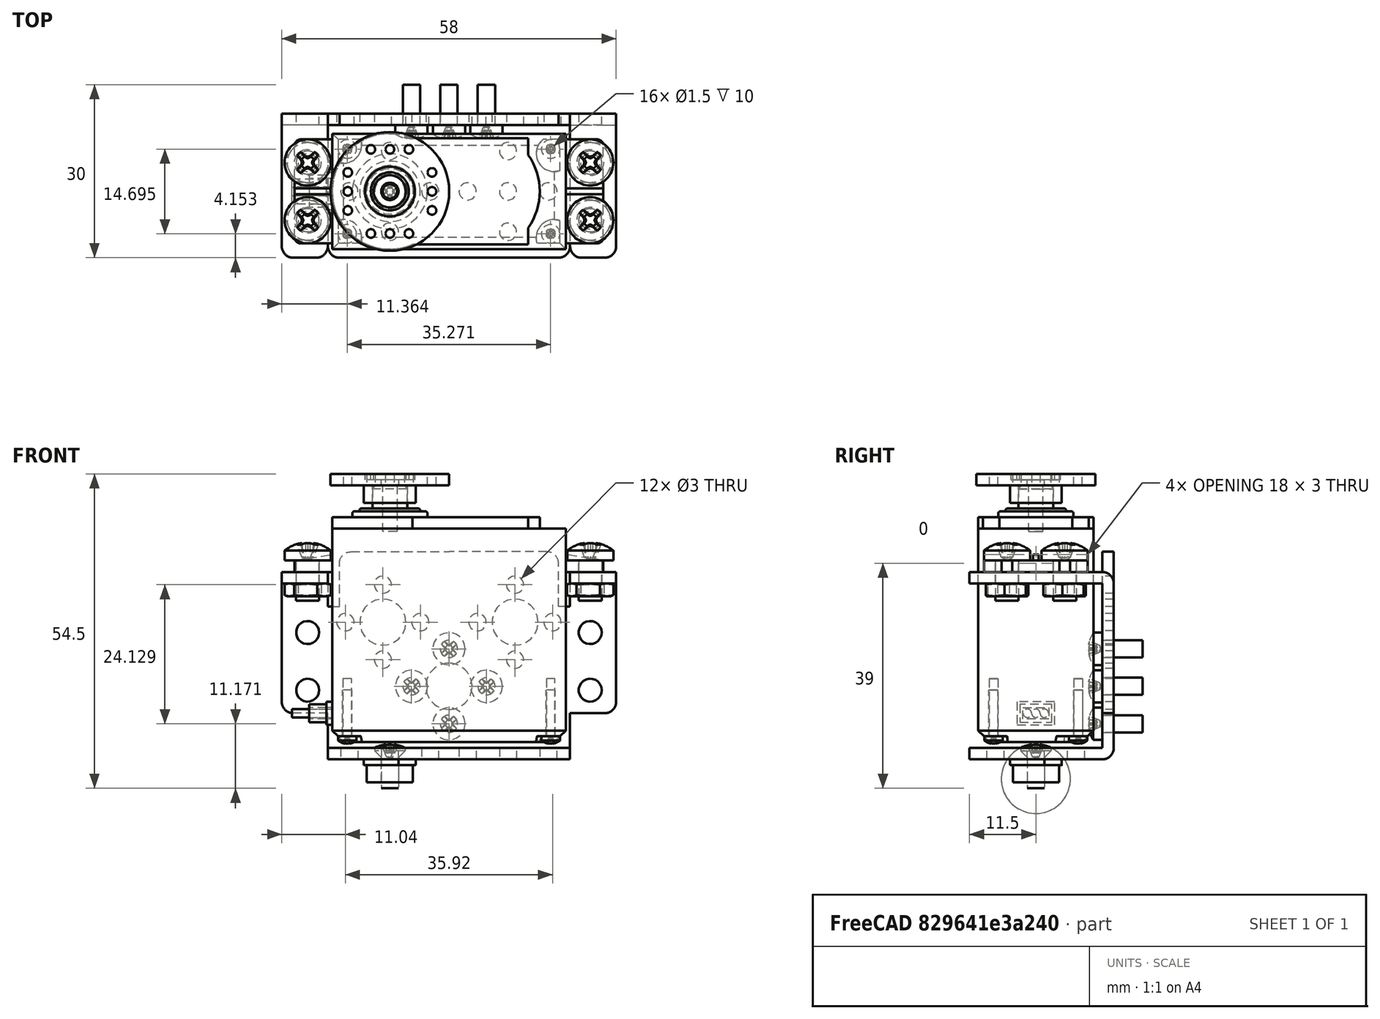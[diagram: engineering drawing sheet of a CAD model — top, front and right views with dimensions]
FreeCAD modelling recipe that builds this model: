
FCSTD DOCUMENT  (FreeCAD 0.19R24276 (Git))
Label: servo_acoplado_1
License: All rights reserved
LicenseURL: http://en.wikipedia.org/wiki/All_rights_reserved
objects: Part::FeaturePython×17, App::FeaturePython×12, App::DocumentObjectGroup×2
note: 17 computed .brp shape members not serialized (recipe doc carries the construction recipe); baked Part::Feature solids carry a one-line shape summary decoded from their .brp

FEATURE [Part::FeaturePython] b_servo_001_  label="servo_001"  # a2plus imported part (geometry in sourceFile) (typed FeaturePython)
  a2p_Version = V0.1
  fixedPosition = true
  objectType = a2pPart
  sourceFile = .\..\piezas\servo.FCStd
  subassemblyImport = false
  timeLastImport = 1.62041e+09
  updateColors = true
FEATURE [Part::FeaturePython] b_parte_servos_001_  label="parte_servos_001"  # a2plus imported part (geometry in sourceFile) (typed FeaturePython)
  Placement = pos=(2.597e-07,13.5,15) rot=(1,0,0;1.5708rad)
  a2p_Version = V0.1
  fixedPosition = false
  objectType = a2pPart
  sourceFile = .\..\piezas\parte_servos.FCStd
  subassemblyImport = false
  timeLastImport = 1.62041e+09
  updateColors = true
FEATURE [Part::FeaturePython] b_arandela_001_  label="arandela_001"  # a2plus imported part (geometry in sourceFile) (typed FeaturePython)
  Placement = pos=(-10.25,3.87576e-07,-3) rot=(0,1,0;3.14159rad)
  a2p_Version = V0.1
  fixedPosition = false
  objectType = a2pPart
  sourceFile = .\..\piezas\arandela.FCStd
  subassemblyImport = false
  timeLastImport = 1.62041e+09
  updateColors = true
FEATURE [Part::FeaturePython] b_tapa_001_  label="tapa_001"  # a2plus imported part (geometry in sourceFile) (typed FeaturePython)
  Placement = pos=(-10.25,-6.8e-14,46.5) rot=(1,0,0;3.14159rad)
  a2p_Version = V0.1
  fixedPosition = false
  objectType = a2pPart
  sourceFile = .\..\piezas\tapa.FCStd
  subassemblyImport = false
  timeLastImport = 1.62041e+09
  updateColors = true
FEATURE [App::FeaturePython] planeCoincident_001  label="planeCoincident_001__parte_servos_001"  # a2plus constraint (typed FeaturePython)
  Object1 = b_servo_001_
  Object2 = b_parte_servos_001_
  ParentTreeObject = -> b_servo_001_
  SubElement1 = Face61
  SubElement2 = Face84
  Suppressed = false
  Type = plane
  directionConstraint = 0
  offset = 0
FEATURE [App::FeaturePython] planeCoincident_001_mirror  label="planeCoincident_001__servo_001"  # a2plus constraint (typed FeaturePython)
  Object1 = b_servo_001_
  Object2 = b_parte_servos_001_
  ParentTreeObject = -> b_parte_servos_001_
  SubElement1 = Face61
  SubElement2 = Face84
  Suppressed = false
  Type = plane
  directionConstraint = 0
  offset = 0
FEATURE [App::FeaturePython] axisCoincident_001  label="axisCoincident_001__parte_servos_001"  # a2plus constraint (typed FeaturePython)
  Object1 = b_servo_001_
  Object2 = b_parte_servos_001_
  ParentTreeObject = -> b_servo_001_
  SubElement1 = Face84
  SubElement2 = Face82
  Suppressed = false
  Type = axial
  directionConstraint = 1
  lockRotation = false
FEATURE [App::FeaturePython] axisCoincident_001_mirror  label="axisCoincident_001__servo_001"  # a2plus constraint (typed FeaturePython)
  Object1 = b_servo_001_
  Object2 = b_parte_servos_001_
  ParentTreeObject = -> b_parte_servos_001_
  SubElement1 = Face84
  SubElement2 = Face82
  Suppressed = false
  Type = axial
  directionConstraint = 1
  lockRotation = false
FEATURE [App::FeaturePython] planeCoincident_002  label="planeCoincident_002__arandela_001"  # a2plus constraint (typed FeaturePython)
  Object1 = b_parte_servos_001_
  Object2 = b_arandela_001_
  ParentTreeObject = -> b_parte_servos_001_
  SubElement1 = Face4
  SubElement2 = Face2
  Suppressed = false
  Type = plane
  directionConstraint = 1
  offset = 0
FEATURE [App::FeaturePython] planeCoincident_002_mirror  label="planeCoincident_002__parte_servos_001"  # a2plus constraint (typed FeaturePython)
  Object1 = b_parte_servos_001_
  Object2 = b_arandela_001_
  ParentTreeObject = -> b_arandela_001_
  SubElement1 = Face4
  SubElement2 = Face2
  Suppressed = false
  Type = plane
  directionConstraint = 1
  offset = 0
FEATURE [App::FeaturePython] axisCoincident_002  label="axisCoincident_002__parte_servos_001"  # a2plus constraint (typed FeaturePython)
  Object1 = b_arandela_001_
  Object2 = b_parte_servos_001_
  ParentTreeObject = -> b_arandela_001_
  SubElement1 = Face4
  SubElement2 = Face17
  Suppressed = false
  Type = axial
  directionConstraint = 1
  lockRotation = false
FEATURE [App::FeaturePython] axisCoincident_002_mirror  label="axisCoincident_002__arandela_001"  # a2plus constraint (typed FeaturePython)
  Object1 = b_arandela_001_
  Object2 = b_parte_servos_001_
  ParentTreeObject = -> b_parte_servos_001_
  SubElement1 = Face4
  SubElement2 = Face17
  Suppressed = false
  Type = axial
  directionConstraint = 1
  lockRotation = false
FEATURE [App::FeaturePython] axisCoincident_003  label="axisCoincident_003__servo_001"  # a2plus constraint (typed FeaturePython)
  Object1 = b_tapa_001_
  Object2 = b_servo_001_
  ParentTreeObject = -> b_tapa_001_
  SubElement1 = Face21
  SubElement2 = Face141
  Suppressed = false
  Type = axial
  directionConstraint = 1
  lockRotation = false
FEATURE [App::FeaturePython] axisCoincident_003_mirror  label="axisCoincident_003__tapa_001"  # a2plus constraint (typed FeaturePython)
  Object1 = b_tapa_001_
  Object2 = b_servo_001_
  ParentTreeObject = -> b_servo_001_
  SubElement1 = Face21
  SubElement2 = Face141
  Suppressed = false
  Type = axial
  directionConstraint = 1
  lockRotation = false
FEATURE [App::FeaturePython] planeCoincident_003  label="planeCoincident_003__servo_001"  # a2plus constraint (typed FeaturePython)
  Object1 = b_tapa_001_
  Object2 = b_servo_001_
  ParentTreeObject = -> b_tapa_001_
  SubElement1 = Face23
  SubElement2 = Face34
  Suppressed = false
  Type = plane
  directionConstraint = 1
  offset = 0
FEATURE [App::FeaturePython] planeCoincident_003_mirror  label="planeCoincident_003__tapa_001"  # a2plus constraint (typed FeaturePython)
  Object1 = b_tapa_001_
  Object2 = b_servo_001_
  ParentTreeObject = -> b_servo_001_
  SubElement1 = Face23
  SubElement2 = Face34
  Suppressed = false
  Type = plane
  directionConstraint = 1
  offset = 0
FEATURE [Part::FeaturePython] Screw  label="M3x7-Screw"  # Fasteners workbench fastener (typed FeaturePython)
  Placement = pos=(-10.25,3.79261e-07,-1) rot=(0,0,1;0rad)
  baseObject = -> b_parte_servos_001_ [Edge75]
  diameter = 4
  invert = false
  length = 11
  lengthCustom = 7
  matchOuter = true
  offset = 0
  thread = false
  type = 36
FEATURE [Part::FeaturePython] Screw001  label="M4x7-Screw"  # Fasteners workbench fastener (typed FeaturePython)
  Placement = pos=(-24.5,5,31.5) rot=(0,0,1;0rad)
  baseObject = -> b_servo_001_ [Edge725]
  diameter = 6
  invert = true
  length = 12
  lengthCustom = 7
  matchOuter = true
  offset = 0
  thread = false
  type = 34
FEATURE [Part::FeaturePython] Screw002  label="M4x7-Screw004"  # Fasteners workbench fastener (typed FeaturePython)
  Placement = pos=(24.5,5,31.5) rot=(0,0,1;0rad)
  baseObject = -> b_servo_001_ [Edge159]
  diameter = 6
  invert = false
  length = 12
  lengthCustom = 7
  matchOuter = true
  offset = 0
  thread = false
  type = 34
FEATURE [Part::FeaturePython] Screw003  label="M4x7-Screw005"  # Fasteners workbench fastener (typed FeaturePython)
  Placement = pos=(24.5,-5,31.5) rot=(0,0,1;0rad)
  baseObject = -> b_servo_001_ [Edge173]
  diameter = 6
  invert = false
  length = 12
  lengthCustom = 7
  matchOuter = true
  offset = 0
  thread = false
  type = 34
FEATURE [Part::FeaturePython] Screw004  label="M4x7-Screw006"  # Fasteners workbench fastener (typed FeaturePython)
  Placement = pos=(-24.5,-5,31.5) rot=(0,0,1;0rad)
  baseObject = -> b_servo_001_ [Edge233]
  diameter = 6
  invert = true
  length = 12
  lengthCustom = 7
  matchOuter = true
  offset = 0
  thread = false
  type = 34
FEATURE [Part::FeaturePython] Nut  label="M4-Nut"  # Fasteners workbench fastener (typed FeaturePython)
  Placement = pos=(-24.5,5,27.5) rot=(-0.456083,0.889937,0;3.14159rad)
  baseObject = -> b_parte_servos_001_ [Edge193]
  diameter = 6
  invert = true
  matchOuter = true
  offset = 0
  thread = false
  type = 9
FEATURE [Part::FeaturePython] Nut001  label="M4-Nut004"  # Fasteners workbench fastener (typed FeaturePython)
  Placement = pos=(-24.5,-5,27.5) rot=(-0.456083,0.889937,0;3.14159rad)
  baseObject = -> b_parte_servos_001_ [Edge192]
  diameter = 6
  invert = true
  matchOuter = true
  offset = 0
  thread = false
  type = 9
FEATURE [Part::FeaturePython] Nut002  label="M4-Nut005"  # Fasteners workbench fastener (typed FeaturePython)
  Placement = pos=(24.5,-5,27.5) rot=(-0.456083,0.889937,0;3.14159rad)
  baseObject = -> b_parte_servos_001_ [Edge219]
  diameter = 6
  invert = true
  matchOuter = true
  offset = 0
  thread = false
  type = 9
FEATURE [Part::FeaturePython] Nut003  label="M4-Nut006"  # Fasteners workbench fastener (typed FeaturePython)
  Placement = pos=(24.5,5,27.5) rot=(-0.456083,0.889937,0;3.14159rad)
  baseObject = -> b_parte_servos_001_ [Edge220]
  diameter = 6
  invert = true
  matchOuter = true
  offset = 0
  thread = false
  type = 9
FEATURE [App::DocumentObjectGroup] Group001  label="tuercas"
  Group = -> [Nut,Nut001,Nut002,Nut003]
FEATURE [Part::FeaturePython] Screw005  label="M3x7-Screw005"  # Fasteners workbench fastener (typed FeaturePython)
  Placement = pos=(2.33689e-07,11.5,16.1711) rot=(1,0,0;1.5708rad)
  baseObject = -> b_parte_servos_001_ [Edge104]
  diameter = 4
  invert = false
  length = 11
  lengthCustom = 7
  matchOuter = true
  offset = 0
  thread = false
  type = 34
FEATURE [Part::FeaturePython] Screw006  label="M3x7-Screw006"  # Fasteners workbench fastener (typed FeaturePython)
  Placement = pos=(-6.5,11.5,9.67113) rot=(1,0,0;1.5708rad)
  baseObject = -> b_parte_servos_001_ [Edge106]
  diameter = 4
  invert = false
  length = 11
  lengthCustom = 7
  matchOuter = true
  offset = 0
  thread = false
  type = 34
FEATURE [Part::FeaturePython] Screw007  label="M3x7-Screw007"  # Fasteners workbench fastener (typed FeaturePython)
  Placement = pos=(4.06088e-07,11.5,3.17113) rot=(1,0,0;1.5708rad)
  baseObject = -> b_parte_servos_001_ [Edge149]
  diameter = 4
  invert = false
  length = 11
  lengthCustom = 7
  matchOuter = true
  offset = 0
  thread = false
  type = 34
FEATURE [Part::FeaturePython] Screw008  label="M3x7-Screw008"  # Fasteners workbench fastener (typed FeaturePython)
  Placement = pos=(6.5,11.5,9.67113) rot=(1,0,0;1.5708rad)
  baseObject = -> b_parte_servos_001_ [Edge154]
  diameter = 4
  invert = false
  length = 11
  lengthCustom = 7
  matchOuter = true
  offset = 0
  thread = false
  type = 34
FEATURE [App::DocumentObjectGroup] Group  label="tornillos"
  Group = -> [Screw,Screw001,Screw002,Screw003,Screw004,Screw005,Screw006,Screw007,Screw008]
